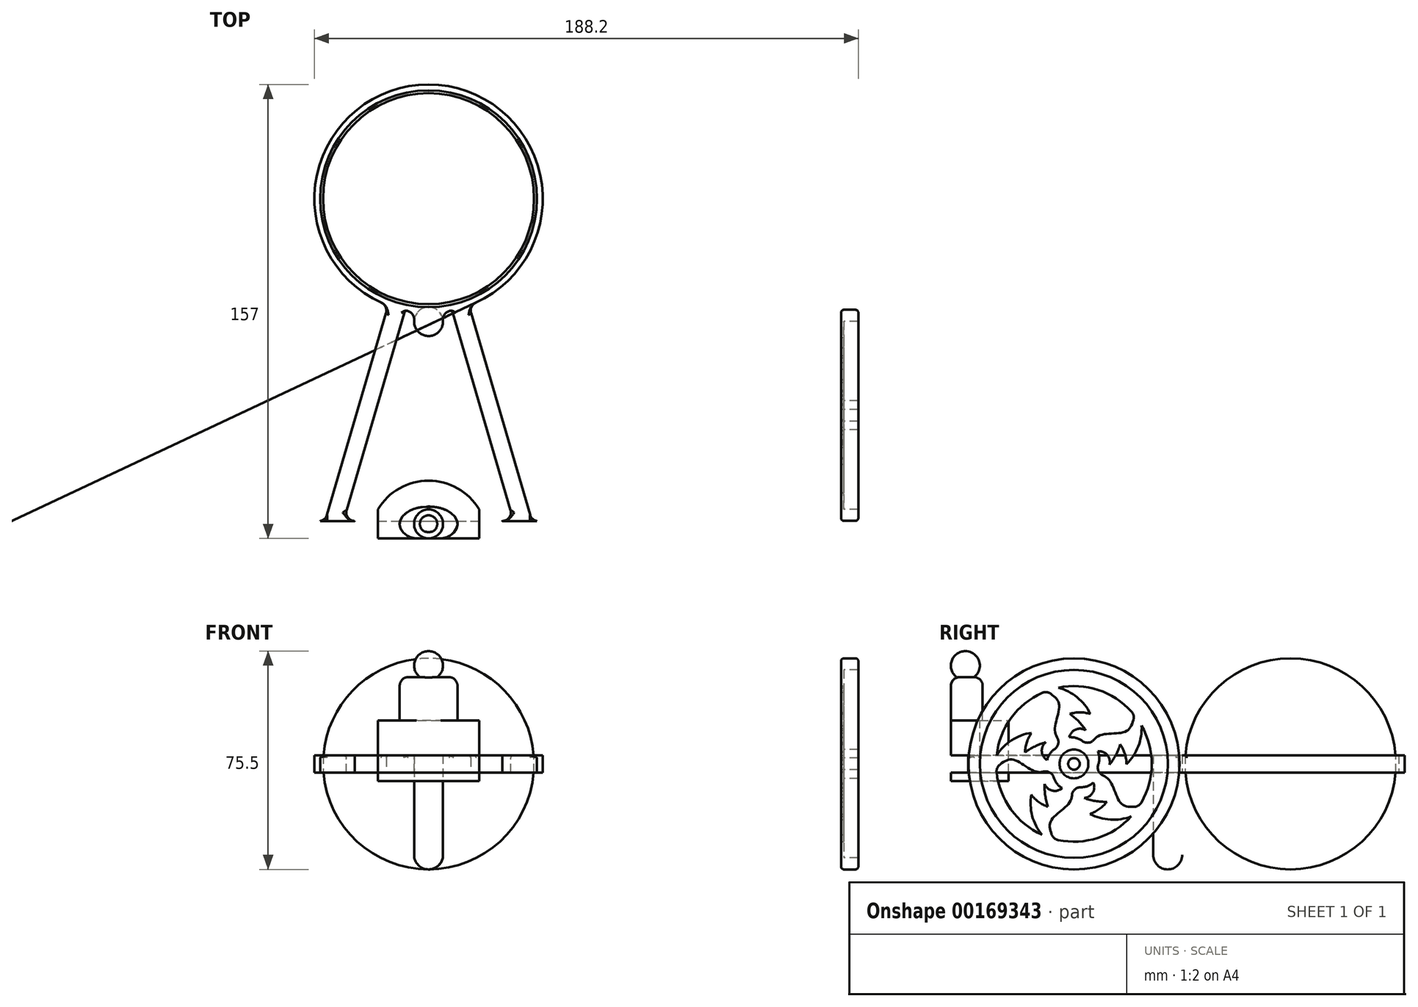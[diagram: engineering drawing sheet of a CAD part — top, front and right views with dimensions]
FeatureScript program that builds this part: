
annotation { "Feature Type Name" : "Feature", "Feature Type Description" : "" }
export const myFeature = defineFeature(function(context is Context, id is Id, definition is map)
    precondition{}
    {
        {
            var Q0;
            Q0=qCreatedBy(makeId("Front.planeOp"),FACE);
            var sketch = newSketch(context, id + "F0", { "sketchPlane" : qUnion([Q0])});
            skArc(sketch, "E0", {"start": v(0, 0) * mm, "mid": v(36.5, 36.5) * mm, "end": v(0, 73) * mm});
            skLineSegment(sketch, "E1", {"start": v(0, 73) * mm, "end": v(0, 0) * mm});
            skSolve(sketch);
        }
        {
            var Q0;
            Q0 = qSketchRegion(id + "F0", true);
            var Q1;
            Q1=sQuery(id+"F0.wireOp",EDGE,"E1");
            revolve(context, id + "F1", {"entities" : qUnion([Q0]), "axis" : qUnion([Q1]), "revolveType" : RevolveType.FULL});
        }
        {
            var Q0;
            Q0=qCreatedBy(makeId("Top.planeOp"),FACE);
            var sketch = newSketch(context, id + "F2", { "sketchPlane" : qUnion([Q0])});
            skCircle(sketch, "E2", {"center": v(0, 0) * mm, "radius": 37.5 * mm});
            skCircle(sketch, "E3.0", {"center": v(0, 0) * mm, "radius": 39.5 * mm});
            skLineSegment(sketch, "E4", {"start": v(0, 0) * mm, "end": v(-33.5, -114.5) * mm});
            skLineSegment(sketch, "E5", {"start": v(-33.5, -114.5) * mm, "end": v(33.5, -114.5) * mm});
            skLineSegment(sketch, "E6", {"start": v(33.5, -114.5) * mm, "end": v(0, 0) * mm});
            skLineSegment(sketch, "E7", {"start": v(0, 0) * mm, "end": v(0, 0) * mm});
            skLineSegment(sketch, "E8", {"start": v(0, 10.68) * mm, "end": v(-37.5, -117.5) * mm});
            skLineSegment(sketch, "E9", {"start": v(-37.5, -117.5) * mm, "end": v(37.5, -117.5) * mm});
            skLineSegment(sketch, "E10", {"start": v(37.5, -117.5) * mm, "end": v(0, 10.68) * mm});
            skLineSegment(sketch, "E11.0", {"start": v(0, -10.68) * mm, "end": v(-29.5, -111.5) * mm});
            skLineSegment(sketch, "E11.1", {"start": v(29.5, -111.5) * mm, "end": v(0, -10.68) * mm});
            skLineSegment(sketch, "E11.2", {"start": v(-29.5, -111.5) * mm, "end": v(29.5, -111.5) * mm});
            skLineSegment(sketch, "E12.top", {"start": v(-37.5, -111.5) * mm, "end": v(37.5, -111.5) * mm});
            skLineSegment(sketch, "E12.left", {"start": v(-37.5, -111.5) * mm, "end": v(-37.5, -117.5) * mm});
            skLineSegment(sketch, "E12.right", {"start": v(37.5, -111.5) * mm, "end": v(37.5, -117.5) * mm});
            skCircle(sketch, "E13", {"center": v(0, -42.5) * mm, "radius": 5 * mm});
            skSolve(sketch);
        }
        {
            var Q0;
            {var subQ0=sQuery(id+"F2.wireOp",EDGE,"E8");var subQ1=sQuery(id+"F2.wireOp",EDGE,"E2");var subQ2=makeQuery(id+"F2.imprint","INTERSECT",VERTEX,{"derivedFrom":[subQ1,subQ0]});Q0=makeQuery(id+"F2.imprint","IMPRINT",FACE,{"disambiguationData":[TD([[makeQuery(id+"F2.imprint","IMPRINT",EDGE,{"disambiguationData":[TD([[subQ2,1.0]])],"derivedFrom":subQ1}),-1.0]])]});}
            var Q1;
            {var subQ0=sQuery(id+"F2.wireOp",EDGE,"E8");var subQ1=sQuery(id+"F2.wireOp",EDGE,"E3.0");var subQ2=makeQuery(id+"F2.imprint","INTERSECT",VERTEX,{"derivedFrom":[subQ1,subQ0]});Q1=makeQuery(id+"F2.imprint","IMPRINT",FACE,{"disambiguationData":[TD([[makeQuery(id+"F2.imprint","IMPRINT",EDGE,{"disambiguationData":[TD([[subQ2,-1.0]])],"derivedFrom":subQ1}),-1.0]])]});}
            var Q2;
            {var subQ0=sQuery(id+"F2.wireOp",EDGE,"E4");var subQ1=sQuery(id+"F2.wireOp",EDGE,"E3.0");var subQ2=makeQuery(id+"F2.imprint","INTERSECT",VERTEX,{"derivedFrom":[subQ1,subQ0]});Q2=makeQuery(id+"F2.imprint","IMPRINT",FACE,{"disambiguationData":[TD([[makeQuery(id+"F2.imprint","IMPRINT",EDGE,{"disambiguationData":[TD([[subQ2,-1.0]])],"derivedFrom":subQ1}),-1.0]])]});}
            var Q3;
            {var subQ0=sQuery(id+"F2.wireOp",EDGE,"E12.left");Q3=makeQuery(id+"F2.imprint","IMPRINT",FACE,{"disambiguationData":[TD([[makeQuery(id+"F2.imprint","IMPRINT",EDGE,{"derivedFrom":subQ0}),1.0]])]});}
            var Q4;
            {var subQ1=sQuery(id+"F2.wireOp",EDGE,"E5");Q4=makeQuery(id+"F2.imprint","IMPRINT",FACE,{"disambiguationData":[TD([[makeQuery(id+"F2.imprint","IMPRINT",EDGE,{"derivedFrom":subQ1}),-1.0]])]});}
            var Q5;
            {var subQ0=sQuery(id+"F2.wireOp",EDGE,"E12.right");Q5=makeQuery(id+"F2.imprint","IMPRINT",FACE,{"disambiguationData":[TD([[makeQuery(id+"F2.imprint","IMPRINT",EDGE,{"derivedFrom":subQ0}),-1.0]])]});}
            var Q6;
            {var subQ1=sQuery(id+"F2.wireOp",EDGE,"E5");Q6=makeQuery(id+"F2.imprint","IMPRINT",FACE,{"disambiguationData":[TD([[makeQuery(id+"F2.imprint","IMPRINT",EDGE,{"derivedFrom":subQ1}),1.0]])]});}
            var Q7;
            {var subQ0=sQuery(id+"F2.wireOp",EDGE,"E11.1");var subQ1=sQuery(id+"F2.wireOp",EDGE,"E3.0");var subQ2=makeQuery(id+"F2.imprint","INTERSECT",VERTEX,{"derivedFrom":[subQ1,subQ0]});Q7=makeQuery(id+"F2.imprint","IMPRINT",FACE,{"disambiguationData":[TD([[makeQuery(id+"F2.imprint","IMPRINT",EDGE,{"disambiguationData":[TD([[subQ2,-1.0]])],"derivedFrom":subQ1}),-1.0]])]});}
            var Q8;
            {var subQ0=sQuery(id+"F2.wireOp",EDGE,"E10");var subQ1=sQuery(id+"F2.wireOp",EDGE,"E3.0");var subQ2=makeQuery(id+"F2.imprint","INTERSECT",VERTEX,{"derivedFrom":[subQ1,subQ0]});Q8=makeQuery(id+"F2.imprint","IMPRINT",FACE,{"disambiguationData":[TD([[makeQuery(id+"F2.imprint","IMPRINT",EDGE,{"disambiguationData":[TD([[subQ2,1.0]])],"derivedFrom":subQ1}),-1.0]])]});}
            var Q9;
            {var subQ0=sQuery(id+"F2.wireOp",EDGE,"E4");var subQ1=sQuery(id+"F2.wireOp",EDGE,"E2");var subQ2=makeQuery(id+"F2.imprint","INTERSECT",VERTEX,{"derivedFrom":[subQ1,subQ0]});Q9=makeQuery(id+"F2.imprint","IMPRINT",FACE,{"disambiguationData":[TD([[makeQuery(id+"F2.imprint","IMPRINT",EDGE,{"disambiguationData":[TD([[subQ2,-1.0]])],"derivedFrom":subQ1}),-1.0]])]});}
            var Q10;
            {var subQ0=sQuery(id+"F2.wireOp",EDGE,"E11.0");var subQ1=sQuery(id+"F2.wireOp",EDGE,"E2");var subQ2=makeQuery(id+"F2.imprint","INTERSECT",VERTEX,{"derivedFrom":[subQ1,subQ0]});Q10=makeQuery(id+"F2.imprint","IMPRINT",FACE,{"disambiguationData":[TD([[makeQuery(id+"F2.imprint","IMPRINT",EDGE,{"disambiguationData":[TD([[subQ2,-1.0]])],"derivedFrom":subQ1}),-1.0]])]});}
            var Q11;
            {var subQ0=sQuery(id+"F2.wireOp",EDGE,"E4");var subQ1=sQuery(id+"F2.wireOp",EDGE,"E2");var subQ2=makeQuery(id+"F2.imprint","INTERSECT",VERTEX,{"derivedFrom":[subQ1,subQ0]});Q11=makeQuery(id+"F2.imprint","IMPRINT",FACE,{"disambiguationData":[TD([[makeQuery(id+"F2.imprint","IMPRINT",EDGE,{"disambiguationData":[TD([[subQ2,1.0]])],"derivedFrom":subQ1}),-1.0]])]});}
            var Q12;
            {var subQ0=sQuery(id+"F2.wireOp",EDGE,"E13");var subQ1=sQuery(id+"F2.wireOp",EDGE,"E2");var subQ2=makeQuery(id+"F2.imprint","INTERSECT",VERTEX,{"derivedFrom":[subQ1,subQ0]});Q12=makeQuery(id+"F2.imprint","IMPRINT",FACE,{"disambiguationData":[TD([[makeQuery(id+"F2.imprint","IMPRINT",EDGE,{"disambiguationData":[TD([[subQ2,-1.0]])],"derivedFrom":subQ1}),-1.0]])]});}
            var Q13;
            {var subQ0=sQuery(id+"F2.wireOp",EDGE,"E13");var subQ1=sQuery(id+"F2.wireOp",EDGE,"E3.0");var subQ2=makeQuery(id+"F2.imprint","INTERSECT",VERTEX,{"disambiguationData":[OD(0.0)],"derivedFrom":[subQ1,subQ0]});Q13=makeQuery(id+"F2.imprint","IMPRINT",FACE,{"disambiguationData":[TD([[makeQuery(id+"F2.imprint","IMPRINT",EDGE,{"disambiguationData":[TD([[subQ2,-1.0]])],"derivedFrom":subQ1}),1.0]])]});}
            var Q14;
            {var subQ0=sQuery(id+"F2.wireOp",EDGE,"E11.1");var subQ1=sQuery(id+"F2.wireOp",EDGE,"E2");var subQ2=makeQuery(id+"F2.imprint","INTERSECT",VERTEX,{"derivedFrom":[subQ1,subQ0]});Q14=makeQuery(id+"F2.imprint","IMPRINT",FACE,{"disambiguationData":[TD([[makeQuery(id+"F2.imprint","IMPRINT",EDGE,{"disambiguationData":[TD([[subQ2,-1.0]])],"derivedFrom":subQ1}),-1.0]])]});}
            var Q15;
            {var subQ0=sQuery(id+"F2.wireOp",EDGE,"E6");var subQ1=sQuery(id+"F2.wireOp",EDGE,"E2");var subQ2=makeQuery(id+"F2.imprint","INTERSECT",VERTEX,{"derivedFrom":[subQ1,subQ0]});Q15=makeQuery(id+"F2.imprint","IMPRINT",FACE,{"disambiguationData":[TD([[makeQuery(id+"F2.imprint","IMPRINT",EDGE,{"disambiguationData":[TD([[subQ2,-1.0]])],"derivedFrom":subQ1}),-1.0]])]});}
            extrude(context, id + "F3", {"entities" : qUnion([Q0, Q1, Q2, Q3, Q4, Q5, Q6, Q7, Q8, Q9, Q10, Q11, Q12, Q13, Q14, Q15]), "depth" : 39.5 * mm, "hasSecondDirection" : true, "secondDirectionOppositeDirection" : false, "secondDirectionDepth" : 33.5 * mm});
        }
        {
            var Q0;
            {var subQ0=sQuery(id+"F2.wireOp",EDGE,"E13");var subQ1=sQuery(id+"F2.wireOp",EDGE,"E3.0");var subQ2=makeQuery(id+"F2.imprint","INTERSECT",VERTEX,{"disambiguationData":[OD(0.0)],"derivedFrom":[subQ1,subQ0]});Q0=makeQuery(id+"F2.imprint","IMPRINT",FACE,{"disambiguationData":[TD([[makeQuery(id+"F2.imprint","IMPRINT",EDGE,{"disambiguationData":[TD([[subQ2,-1.0]])],"derivedFrom":subQ1}),-1.0]])]});}
            var Q1;
            {var subQ0=sQuery(id+"F2.wireOp",EDGE,"E13");var subQ1=sQuery(id+"F2.wireOp",EDGE,"E3.0");var subQ2=makeQuery(id+"F2.imprint","INTERSECT",VERTEX,{"disambiguationData":[OD(0.0)],"derivedFrom":[subQ1,subQ0]});Q1=makeQuery(id+"F2.imprint","IMPRINT",FACE,{"disambiguationData":[TD([[makeQuery(id+"F2.imprint","IMPRINT",EDGE,{"disambiguationData":[TD([[subQ2,-1.0]])],"derivedFrom":subQ1}),1.0]])]});}
            extrude(context, id + "F4", {"entities" : qUnion([Q0, Q1]), "operationType" : NewBodyOperationType.ADD, "depth" : 39.5 * mm});
        }
        {
            var Q0;
            Q0=makeQuery(id+"F4.opExtrude","CAP_EDGE",EDGE,{"disambiguationData":[OSD([sQuery(id+"F2.wireOp",EDGE,"E13")])],"isStart":true});
            fillet(context, id + "F5", {"entities" : qUnion([Q0]), "radius" : 5 * mm, "tangentPropagation" : true, "allowEdgeOverflow" : false});
        }
        {
            var Q0;
            Q0=qCreatedBy(makeId("Right.planeOp"),FACE);
            var sketch = newSketch(context, id + "F6", { "sketchPlane" : qUnion([Q0])});
            skCircle(sketch, "E14", {"center": v(-114.5, 36.5) * mm, "radius": 36.5 * mm});
            skCircle(sketch, "E15", {"center": v(-114.5, 36.5) * mm, "radius": 1.9 * mm});
            skLineSegment(sketch, "E16", {"start": v(-114.5, 36.5) * mm, "end": v(-114.5, 41.97) * mm, "construction": true});
            skLineSegment(sketch, "E17", {"start": v(-114.5, 36.5) * mm, "end": v(-121.58, 36.5) * mm, "construction": true});
            skSolve(sketch);
        }
        {
            var Q0;
            Q0=makeQuery(id+"F6.imprint","IMPRINT",FACE,{"disambiguationData":[TD([[makeQuery(id+"F6.imprint","IMPRINT",EDGE,{"derivedFrom":sQuery(id+"F6.wireOp",EDGE,"E15")}),1.0]])]});
            extrude(context, id + "F7", {"entities" : qUnion([Q0]), "operationType" : NewBodyOperationType.ADD, "depth" : 45.5 * mm, "hasSecondDirection" : true, "secondDirectionOppositeDirection" : true, "secondDirectionDepth" : 45.5 * mm});
        }
        {
            var Q0;
            Q0=makeQuery(id+"F3.opExtrude","CAP_FACE",FACE,{"disambiguationData":[OSD([sQuery(id+"F2.wireOp",EDGE,"E2"),sQuery(id+"F2.wireOp",EDGE,"E3.0"),sQuery(id+"F2.wireOp",EDGE,"E8"),sQuery(id+"F2.wireOp",EDGE,"E10"),sQuery(id+"F2.wireOp",EDGE,"E11.0"),sQuery(id+"F2.wireOp",EDGE,"E11.1"),sQuery(id+"F2.wireOp",EDGE,"E9"),sQuery(id+"F2.wireOp",EDGE,"E12.top"),sQuery(id+"F2.wireOp",EDGE,"E12.left"),sQuery(id+"F2.wireOp",EDGE,"E12.right")])],"isStart":true});
            var Q1;
            Q1=makeQuery(id+"F4.boolean.opBoolean","MERGE",FACE,{"derivedFrom":[makeQuery(id+"F3.opExtrude","CAP_FACE",FACE,{"disambiguationData":[OSD([sQuery(id+"F2.wireOp",EDGE,"E2"),sQuery(id+"F2.wireOp",EDGE,"E3.0"),sQuery(id+"F2.wireOp",EDGE,"E8"),sQuery(id+"F2.wireOp",EDGE,"E10"),sQuery(id+"F2.wireOp",EDGE,"E11.0"),sQuery(id+"F2.wireOp",EDGE,"E11.1"),sQuery(id+"F2.wireOp",EDGE,"E9"),sQuery(id+"F2.wireOp",EDGE,"E12.top"),sQuery(id+"F2.wireOp",EDGE,"E12.left"),sQuery(id+"F2.wireOp",EDGE,"E12.right")])],"isStart":false}),makeQuery(id+"F4.opExtrude","CAP_FACE",FACE,{"disambiguationData":[OSD([sQuery(id+"F2.wireOp",EDGE,"E13")])],"isStart":false})]});
            cPlane(context, id + "F8", {"entities" : qUnion([Q0, Q1]), "cplaneType" : CPlaneType.MID_PLANE, "offset" : 25.4 * mm, "width" : 152.4 * mm, "height" : 152.4 * mm});
        }
        {
            var Q0;
            Q0=qCreatedBy(makeId("Right.planeOp"),FACE);
            var sketch = newSketch(context, id + "F9", { "sketchPlane" : qUnion([Q0])});
            skCircle(sketch, "E18", {"center": v(-114.5, 36.5) * mm, "radius": 2.25 * mm});
            skLineSegment(sketch, "E19", {"start": v(-116.25, 37.92) * mm, "end": v(-112.75, 37.92) * mm});
            skLineSegment(sketch, "E20", {"start": v(-116.47, 35.42) * mm, "end": v(-112.53, 35.42) * mm});
            skLineSegment(sketch, "E21", {"start": v(-115, 38.7) * mm, "end": v(-115, 34.3) * mm});
            skLineSegment(sketch, "E22", {"start": v(-114, 38.7) * mm, "end": v(-114, 34.3) * mm});
            skLineSegment(sketch, "E23", {"start": v(-114.5, 36.5) * mm, "end": v(-114.5, 31.41) * mm, "construction": true});
            skSolve(sketch);
        }
        {
            var Q0;
            {var subQ0=sQuery(id+"F9.wireOp",EDGE,"E19");var subQ1=sQuery(id+"F9.wireOp",EDGE,"E18");var subQ2=makeQuery(id+"F9.imprint","INTERSECT",VERTEX,{"disambiguationData":[OD(0.0)],"derivedFrom":[subQ1,subQ0]});Q0=makeQuery(id+"F9.imprint","IMPRINT",FACE,{"disambiguationData":[TD([[makeQuery(id+"F9.imprint","IMPRINT",EDGE,{"disambiguationData":[TD([[subQ2,-1.0]])],"derivedFrom":subQ1}),1.0]])]});}
            var Q1;
            {var subQ0=sQuery(id+"F9.wireOp",EDGE,"E19");var subQ1=sQuery(id+"F9.wireOp",EDGE,"E18");var subQ2=makeQuery(id+"F9.imprint","INTERSECT",VERTEX,{"disambiguationData":[OD(1.0)],"derivedFrom":[subQ1,subQ0]});Q1=makeQuery(id+"F9.imprint","IMPRINT",FACE,{"disambiguationData":[TD([[makeQuery(id+"F9.imprint","IMPRINT",EDGE,{"disambiguationData":[TD([[subQ2,1.0]])],"derivedFrom":subQ1}),1.0]])]});}
            var Q2;
            {var subQ0=sQuery(id+"F9.wireOp",EDGE,"E21");var subQ1=sQuery(id+"F9.wireOp",EDGE,"E19");var subQ2=makeQuery(id+"F9.imprint","INTERSECT",VERTEX,{"derivedFrom":[subQ1,subQ0]});Q2=makeQuery(id+"F9.imprint","IMPRINT",FACE,{"disambiguationData":[TD([[makeQuery(id+"F9.imprint","IMPRINT",EDGE,{"disambiguationData":[TD([[subQ2,-1.0]])],"derivedFrom":subQ1}),-1.0]])]});}
            var Q3;
            Q3=makeQuery(id+"F7.opExtrude","CAP_FACE",FACE,{"disambiguationData":[OSD([sQuery(id+"F6.wireOp",EDGE,"E15")])],"isStart":false});
            extrude(context, id + "F10", {"entities" : qUnion([Q0, Q1, Q2]), "operationType" : NewBodyOperationType.ADD, "endBound" : BoundingType.UP_TO_SURFACE, "endBoundEntityFace" : qUnion([Q3]), "depth" : 25.4 * mm, "hasSecondDirection" : true, "secondDirectionOppositeDirection" : false, "secondDirectionDepth" : 44 * mm});
        }
        {
            var Q0;
            {var subQ0=sQuery(id+"F9.wireOp",EDGE,"E19");var subQ1=sQuery(id+"F9.wireOp",EDGE,"E18");var subQ2=makeQuery(id+"F9.imprint","INTERSECT",VERTEX,{"disambiguationData":[OD(0.0)],"derivedFrom":[subQ1,subQ0]});Q0=makeQuery(id+"F9.imprint","IMPRINT",FACE,{"disambiguationData":[TD([[makeQuery(id+"F9.imprint","IMPRINT",EDGE,{"disambiguationData":[TD([[subQ2,-1.0]])],"derivedFrom":subQ1}),1.0]])]});}
            var Q1;
            {var subQ0=sQuery(id+"F9.wireOp",EDGE,"E21");var subQ1=sQuery(id+"F9.wireOp",EDGE,"E19");var subQ2=makeQuery(id+"F9.imprint","INTERSECT",VERTEX,{"derivedFrom":[subQ1,subQ0]});Q1=makeQuery(id+"F9.imprint","IMPRINT",FACE,{"disambiguationData":[TD([[makeQuery(id+"F9.imprint","IMPRINT",EDGE,{"disambiguationData":[TD([[subQ2,-1.0]])],"derivedFrom":subQ1}),-1.0]])]});}
            var Q2;
            {var subQ0=sQuery(id+"F9.wireOp",EDGE,"E19");var subQ1=sQuery(id+"F9.wireOp",EDGE,"E18");var subQ2=makeQuery(id+"F9.imprint","INTERSECT",VERTEX,{"disambiguationData":[OD(1.0)],"derivedFrom":[subQ1,subQ0]});Q2=makeQuery(id+"F9.imprint","IMPRINT",FACE,{"disambiguationData":[TD([[makeQuery(id+"F9.imprint","IMPRINT",EDGE,{"disambiguationData":[TD([[subQ2,1.0]])],"derivedFrom":subQ1}),1.0]])]});}
            var Q3;
            Q3=makeQuery(id+"F7.opExtrude","CAP_FACE",FACE,{"disambiguationData":[OSD([sQuery(id+"F6.wireOp",EDGE,"E15")])],"isStart":true});
            extrude(context, id + "F11", {"entities" : qUnion([Q0, Q1, Q2]), "operationType" : NewBodyOperationType.ADD, "endBound" : BoundingType.UP_TO_SURFACE, "oppositeDirection" : true, "endBoundEntityFace" : qUnion([Q3]), "depth" : 25.4 * mm, "hasSecondDirection" : true, "secondDirectionOppositeDirection" : true, "secondDirectionDepth" : 44 * mm});
        }
        {
            var Q0;
            {var subQ0=sQuery(id+"F9.wireOp",EDGE,"E21");var subQ1=sQuery(id+"F9.wireOp",EDGE,"E18");var subQ2=makeQuery(id+"F9.imprint","INTERSECT",VERTEX,{"disambiguationData":[OD(0.0)],"derivedFrom":[subQ1,subQ0]});Q0=makeQuery(id+"F9.imprint","IMPRINT",FACE,{"disambiguationData":[TD([[makeQuery(id+"F9.imprint","IMPRINT",EDGE,{"disambiguationData":[TD([[subQ2,1.0]])],"derivedFrom":subQ1}),1.0]])]});}
            var Q1;
            {var subQ0=sQuery(id+"F9.wireOp",EDGE,"E21");var subQ1=sQuery(id+"F9.wireOp",EDGE,"E19");var subQ2=makeQuery(id+"F9.imprint","INTERSECT",VERTEX,{"derivedFrom":[subQ1,subQ0]});Q1=makeQuery(id+"F9.imprint","IMPRINT",FACE,{"disambiguationData":[TD([[makeQuery(id+"F9.imprint","IMPRINT",EDGE,{"disambiguationData":[TD([[subQ2,-1.0]])],"derivedFrom":subQ1}),-1.0]])]});}
            var Q2;
            {var subQ0=sQuery(id+"F9.wireOp",EDGE,"E21");var subQ1=sQuery(id+"F9.wireOp",EDGE,"E18");var subQ2=makeQuery(id+"F9.imprint","INTERSECT",VERTEX,{"disambiguationData":[OD(1.0)],"derivedFrom":[subQ1,subQ0]});Q2=makeQuery(id+"F9.imprint","IMPRINT",FACE,{"disambiguationData":[TD([[makeQuery(id+"F9.imprint","IMPRINT",EDGE,{"disambiguationData":[TD([[subQ2,-1.0]])],"derivedFrom":subQ1}),1.0]])]});}
            var Q3;
            Q3=makeQuery(id+"F10.boolean.opBoolean","MERGE",FACE,{"derivedFrom":[makeQuery(id+"F7.opExtrude","CAP_FACE",FACE,{"disambiguationData":[OSD([sQuery(id+"F6.wireOp",EDGE,"E15")])],"isStart":false}),makeQuery(id+"F10.opExtrude","CAP_FACE",FACE,{"disambiguationData":[OSD([sQuery(id+"F9.wireOp",EDGE,"E18"),sQuery(id+"F9.wireOp",EDGE,"E19"),sQuery(id+"F9.wireOp",EDGE,"E20")])],"isStart":false})]});
            extrude(context, id + "F12", {"entities" : qUnion([Q0, Q1, Q2]), "operationType" : NewBodyOperationType.REMOVE, "endBound" : BoundingType.UP_TO_SURFACE, "endBoundEntityFace" : qUnion([Q3]), "depth" : 25.4 * mm, "hasSecondDirection" : true, "secondDirectionOppositeDirection" : false, "secondDirectionDepth" : 40 * mm});
        }
        {
            var Q0;
            {var subQ0=sQuery(id+"F9.wireOp",EDGE,"E21");var subQ1=sQuery(id+"F9.wireOp",EDGE,"E18");var subQ2=makeQuery(id+"F9.imprint","INTERSECT",VERTEX,{"disambiguationData":[OD(0.0)],"derivedFrom":[subQ1,subQ0]});Q0=makeQuery(id+"F9.imprint","IMPRINT",FACE,{"disambiguationData":[TD([[makeQuery(id+"F9.imprint","IMPRINT",EDGE,{"disambiguationData":[TD([[subQ2,1.0]])],"derivedFrom":subQ1}),1.0]])]});}
            var Q1;
            {var subQ0=sQuery(id+"F9.wireOp",EDGE,"E21");var subQ1=sQuery(id+"F9.wireOp",EDGE,"E19");var subQ2=makeQuery(id+"F9.imprint","INTERSECT",VERTEX,{"derivedFrom":[subQ1,subQ0]});Q1=makeQuery(id+"F9.imprint","IMPRINT",FACE,{"disambiguationData":[TD([[makeQuery(id+"F9.imprint","IMPRINT",EDGE,{"disambiguationData":[TD([[subQ2,-1.0]])],"derivedFrom":subQ1}),-1.0]])]});}
            var Q2;
            {var subQ0=sQuery(id+"F9.wireOp",EDGE,"E21");var subQ1=sQuery(id+"F9.wireOp",EDGE,"E18");var subQ2=makeQuery(id+"F9.imprint","INTERSECT",VERTEX,{"disambiguationData":[OD(1.0)],"derivedFrom":[subQ1,subQ0]});Q2=makeQuery(id+"F9.imprint","IMPRINT",FACE,{"disambiguationData":[TD([[makeQuery(id+"F9.imprint","IMPRINT",EDGE,{"disambiguationData":[TD([[subQ2,-1.0]])],"derivedFrom":subQ1}),1.0]])]});}
            var Q3;
            Q3=makeQuery(id+"F11.boolean.opBoolean","MERGE",FACE,{"derivedFrom":[makeQuery(id+"F7.opExtrude","CAP_FACE",FACE,{"disambiguationData":[OSD([sQuery(id+"F6.wireOp",EDGE,"E15")])],"isStart":true}),makeQuery(id+"F11.opExtrude","CAP_FACE",FACE,{"disambiguationData":[OSD([sQuery(id+"F9.wireOp",EDGE,"E18"),sQuery(id+"F9.wireOp",EDGE,"E19"),sQuery(id+"F9.wireOp",EDGE,"E20")])],"isStart":false})]});
            extrude(context, id + "F13", {"entities" : qUnion([Q0, Q1, Q2]), "operationType" : NewBodyOperationType.REMOVE, "endBound" : BoundingType.UP_TO_SURFACE, "oppositeDirection" : true, "endBoundEntityFace" : qUnion([Q3]), "depth" : 25.4 * mm, "hasSecondDirection" : true, "secondDirectionOppositeDirection" : true, "secondDirectionDepth" : 40 * mm});
        }
        {
            var Q0;
            Q0=makeQuery(id+"F3.opExtrude","CAP_EDGE",EDGE,{"disambiguationData":[OSD([sQuery(id+"F2.wireOp",EDGE,"E9")])],"isStart":false});
            var Q1;
            {var subQ0=sQuery(id+"F2.wireOp",EDGE,"E12.top");Q1=makeQuery(id+"F3.opExtrude","CAP_EDGE",EDGE,{"disambiguationData":[OSD([subQ0]),TDD([makeQuery(id+"F2.imprint","IMPRINT",EDGE,{"disambiguationData":[TD([[makeQuery(id+"F2.imprint","INTERSECT",VERTEX,{"derivedFrom":[sQuery(id+"F2.wireOp",EDGE,"E11.0"),subQ0]}),-1.0]])],"derivedFrom":subQ0})])],"isStart":false});}
            var Q2;
            {var subQ0=sQuery(id+"F2.wireOp",EDGE,"E12.top");Q2=makeQuery(id+"F3.opExtrude","CAP_EDGE",EDGE,{"disambiguationData":[OSD([subQ0]),TDD([makeQuery(id+"F2.imprint","IMPRINT",EDGE,{"disambiguationData":[TD([[makeQuery(id+"F2.imprint","INTERSECT",VERTEX,{"derivedFrom":[subQ0,sQuery(id+"F2.wireOp",EDGE,"E12.left")]}),-1.0]])],"derivedFrom":subQ0})])],"isStart":false});}
            var Q3;
            {var subQ0=sQuery(id+"F2.wireOp",EDGE,"E12.top");Q3=makeQuery(id+"F3.opExtrude","CAP_EDGE",EDGE,{"disambiguationData":[OSD([subQ0]),TDD([makeQuery(id+"F2.imprint","IMPRINT",EDGE,{"disambiguationData":[TD([[makeQuery(id+"F2.imprint","INTERSECT",VERTEX,{"derivedFrom":[subQ0,sQuery(id+"F2.wireOp",EDGE,"E12.right")]}),1.0]])],"derivedFrom":subQ0})])],"isStart":false});}
            var Q4;
            Q4=makeQuery(id+"F3.opExtrude","CAP_EDGE",EDGE,{"disambiguationData":[OSD([sQuery(id+"F2.wireOp",EDGE,"E10")])],"isStart":false});
            var Q5;
            Q5=makeQuery(id+"F3.opExtrude","CAP_EDGE",EDGE,{"disambiguationData":[OSD([sQuery(id+"F2.wireOp",EDGE,"E11.1")])],"isStart":false});
            var Q6;
            Q6=makeQuery(id+"F3.opExtrude","CAP_EDGE",EDGE,{"disambiguationData":[OSD([sQuery(id+"F2.wireOp",EDGE,"E8")])],"isStart":false});
            var Q7;
            Q7=makeQuery(id+"F3.opExtrude","CAP_EDGE",EDGE,{"disambiguationData":[OSD([sQuery(id+"F2.wireOp",EDGE,"E11.0")])],"isStart":false});
            fillet(context, id + "F14", {"entities" : qUnion([Q0, Q1, Q2, Q3, Q4, Q5, Q6, Q7]), "radius" : 1 * mm, "tangentPropagation" : true, "allowEdgeOverflow" : false});
        }
        {
            var Q0;
            {var subQ0=sQuery(id+"F2.wireOp",EDGE,"E13");var subQ1=sQuery(id+"F2.wireOp",EDGE,"E3.0");var subQ2=makeQuery(id+"F2.imprint","INTERSECT",VERTEX,{"disambiguationData":[OD(1.0)],"derivedFrom":[subQ1,subQ0]});var subQ3=makeQuery(id+"F2.imprint","INTERSECT",VERTEX,{"disambiguationData":[OD(0.0)],"derivedFrom":[subQ1,subQ0]});Q0=makeQuery(id+"F4.boolean.opBoolean","INTERSECT",EDGE,{"disambiguationData":[OD(0.0)],"derivedFrom":[makeQuery(id+"F3.opExtrude","SWEPT_FACE",FACE,{"disambiguationData":[OSD([subQ1]),TDD([makeQuery(id+"F2.imprint","IMPRINT",EDGE,{"disambiguationData":[TD([[makeQuery(id+"F2.imprint","INTERSECT",VERTEX,{"derivedFrom":[subQ1,sQuery(id+"F2.wireOp",EDGE,"E11.0")]}),-1.0]])],"derivedFrom":subQ1}),makeQuery(id+"F2.imprint","IMPRINT",EDGE,{"disambiguationData":[TD([[subQ3,-1.0]])],"derivedFrom":subQ1}),makeQuery(id+"F2.imprint","IMPRINT",EDGE,{"disambiguationData":[TD([[subQ2,-1.0]])],"derivedFrom":subQ1})])]}),makeQuery(id+"F4.opExtrude","SWEPT_FACE",FACE,{"disambiguationData":[OSD([subQ0])]})]});}
            var Q1;
            {var subQ0=sQuery(id+"F2.wireOp",EDGE,"E13");var subQ1=sQuery(id+"F2.wireOp",EDGE,"E3.0");var subQ2=makeQuery(id+"F2.imprint","INTERSECT",VERTEX,{"disambiguationData":[OD(1.0)],"derivedFrom":[subQ1,subQ0]});var subQ3=makeQuery(id+"F2.imprint","INTERSECT",VERTEX,{"disambiguationData":[OD(0.0)],"derivedFrom":[subQ1,subQ0]});Q1=makeQuery(id+"F4.boolean.opBoolean","INTERSECT",EDGE,{"disambiguationData":[OD(1.0)],"derivedFrom":[makeQuery(id+"F3.opExtrude","SWEPT_FACE",FACE,{"disambiguationData":[OSD([subQ1]),TDD([makeQuery(id+"F2.imprint","IMPRINT",EDGE,{"disambiguationData":[TD([[makeQuery(id+"F2.imprint","INTERSECT",VERTEX,{"derivedFrom":[subQ1,sQuery(id+"F2.wireOp",EDGE,"E11.0")]}),-1.0]])],"derivedFrom":subQ1}),makeQuery(id+"F2.imprint","IMPRINT",EDGE,{"disambiguationData":[TD([[subQ3,-1.0]])],"derivedFrom":subQ1}),makeQuery(id+"F2.imprint","IMPRINT",EDGE,{"disambiguationData":[TD([[subQ2,-1.0]])],"derivedFrom":subQ1})])]}),makeQuery(id+"F4.opExtrude","SWEPT_FACE",FACE,{"disambiguationData":[OSD([subQ0])]})]});}
            fillet(context, id + "F15", {"entities" : qUnion([Q0, Q1]), "radius" : 3 * mm, "tangentPropagation" : true, "allowEdgeOverflow" : false});
        }
        {
            var Q0;
            Q0=makeQuery(id+"F3.opExtrude","SWEPT_EDGE",EDGE,{"disambiguationData":[OSD([sQuery(id+"F2.wireOp",EDGE,"E11.0"),sQuery(id+"F2.wireOp",EDGE,"E12.top")])]});
            var Q1;
            Q1=makeQuery(id+"F3.opExtrude","SWEPT_EDGE",EDGE,{"disambiguationData":[OSD([sQuery(id+"F2.wireOp",EDGE,"E11.1"),sQuery(id+"F2.wireOp",EDGE,"E12.top")])]});
            var Q2;
            Q2=makeQuery(id+"F3.opExtrude","SWEPT_EDGE",EDGE,{"disambiguationData":[OSD([sQuery(id+"F2.wireOp",EDGE,"E10"),sQuery(id+"F2.wireOp",EDGE,"E12.top")])]});
            var Q3;
            Q3=makeQuery(id+"F3.opExtrude","SWEPT_EDGE",EDGE,{"disambiguationData":[OSD([sQuery(id+"F2.wireOp",EDGE,"E8"),sQuery(id+"F2.wireOp",EDGE,"E12.top")])]});
            var Q4;
            Q4=makeQuery(id+"F3.opExtrude","SWEPT_EDGE",EDGE,{"disambiguationData":[OSD([sQuery(id+"F2.wireOp",EDGE,"E3.0"),sQuery(id+"F2.wireOp",EDGE,"E10")])]});
            var Q5;
            Q5=makeQuery(id+"F3.opExtrude","SWEPT_EDGE",EDGE,{"disambiguationData":[OSD([sQuery(id+"F2.wireOp",EDGE,"E3.0"),sQuery(id+"F2.wireOp",EDGE,"E8")])]});
            fillet(context, id + "F16", {"entities" : qUnion([Q0, Q1, Q2, Q3, Q4, Q5]), "radius" : 3 * mm, "tangentPropagation" : true, "allowEdgeOverflow" : false});
        }
        {
            var Q0;
            Q0=makeQuery(id+"F3.opExtrude","SWEPT_EDGE",EDGE,{"disambiguationData":[OSD([sQuery(id+"F2.wireOp",EDGE,"E3.0"),sQuery(id+"F2.wireOp",EDGE,"E11.0")])]});
            var Q1;
            Q1=makeQuery(id+"F3.opExtrude","SWEPT_EDGE",EDGE,{"disambiguationData":[OSD([sQuery(id+"F2.wireOp",EDGE,"E3.0"),sQuery(id+"F2.wireOp",EDGE,"E11.1")])]});
            fillet(context, id + "F17", {"entities" : qUnion([Q0, Q1]), "radius" : 1 * mm, "tangentPropagation" : true, "allowEdgeOverflow" : false});
        }
        {
            var Q0;
            {var subQ0=sQuery(id+"F9.wireOp",EDGE,"E18");Q0=makeQuery(id+"F10.opExtrude","CAP_EDGE",EDGE,{"disambiguationData":[OSD([subQ0]),TDD([makeQuery(id+"F9.imprint","IMPRINT",EDGE,{"disambiguationData":[TD([[makeQuery(id+"F9.imprint","INTERSECT",VERTEX,{"disambiguationData":[OD(0.0)],"derivedFrom":[subQ0,sQuery(id+"F9.wireOp",EDGE,"E19")]}),-1.0]])],"derivedFrom":subQ0})])],"isStart":false});}
            var Q1;
            {var subQ0=sQuery(id+"F9.wireOp",EDGE,"E18");Q1=makeQuery(id+"F10.opExtrude","CAP_EDGE",EDGE,{"disambiguationData":[OSD([subQ0]),TDD([makeQuery(id+"F9.imprint","IMPRINT",EDGE,{"disambiguationData":[TD([[makeQuery(id+"F9.imprint","INTERSECT",VERTEX,{"disambiguationData":[OD(1.0)],"derivedFrom":[subQ0,sQuery(id+"F9.wireOp",EDGE,"E19")]}),1.0]])],"derivedFrom":subQ0})])],"isStart":false});}
            var Q2;
            {var subQ0=sQuery(id+"F9.wireOp",EDGE,"E18");Q2=makeQuery(id+"F10.opExtrude","CAP_EDGE",EDGE,{"disambiguationData":[OSD([subQ0]),TDD([makeQuery(id+"F9.imprint","IMPRINT",EDGE,{"disambiguationData":[TD([[makeQuery(id+"F9.imprint","INTERSECT",VERTEX,{"disambiguationData":[OD(0.0)],"derivedFrom":[subQ0,sQuery(id+"F9.wireOp",EDGE,"E19")]}),-1.0]])],"derivedFrom":subQ0})])],"isStart":true});}
            var Q3;
            {var subQ0=sQuery(id+"F9.wireOp",EDGE,"E18");Q3=makeQuery(id+"F10.opExtrude","CAP_EDGE",EDGE,{"disambiguationData":[OSD([subQ0]),TDD([makeQuery(id+"F9.imprint","IMPRINT",EDGE,{"disambiguationData":[TD([[makeQuery(id+"F9.imprint","INTERSECT",VERTEX,{"disambiguationData":[OD(1.0)],"derivedFrom":[subQ0,sQuery(id+"F9.wireOp",EDGE,"E19")]}),1.0]])],"derivedFrom":subQ0})])],"isStart":true});}
            var Q4;
            {var subQ0=sQuery(id+"F9.wireOp",EDGE,"E18");Q4=makeQuery(id+"F11.opExtrude","CAP_EDGE",EDGE,{"disambiguationData":[OSD([subQ0]),TDD([makeQuery(id+"F9.imprint","IMPRINT",EDGE,{"disambiguationData":[TD([[makeQuery(id+"F9.imprint","INTERSECT",VERTEX,{"disambiguationData":[OD(0.0)],"derivedFrom":[subQ0,sQuery(id+"F9.wireOp",EDGE,"E19")]}),-1.0]])],"derivedFrom":subQ0})])],"isStart":false});}
            var Q5;
            {var subQ0=sQuery(id+"F9.wireOp",EDGE,"E18");Q5=makeQuery(id+"F11.opExtrude","CAP_EDGE",EDGE,{"disambiguationData":[OSD([subQ0]),TDD([makeQuery(id+"F9.imprint","IMPRINT",EDGE,{"disambiguationData":[TD([[makeQuery(id+"F9.imprint","INTERSECT",VERTEX,{"disambiguationData":[OD(0.0)],"derivedFrom":[subQ0,sQuery(id+"F9.wireOp",EDGE,"E19")]}),-1.0]])],"derivedFrom":subQ0})])],"isStart":true});}
            var Q6;
            {var subQ0=sQuery(id+"F9.wireOp",EDGE,"E18");Q6=makeQuery(id+"F11.opExtrude","CAP_EDGE",EDGE,{"disambiguationData":[OSD([subQ0]),TDD([makeQuery(id+"F9.imprint","IMPRINT",EDGE,{"disambiguationData":[TD([[makeQuery(id+"F9.imprint","INTERSECT",VERTEX,{"disambiguationData":[OD(1.0)],"derivedFrom":[subQ0,sQuery(id+"F9.wireOp",EDGE,"E19")]}),1.0]])],"derivedFrom":subQ0})])],"isStart":false});}
            var Q7;
            {var subQ0=sQuery(id+"F9.wireOp",EDGE,"E18");Q7=makeQuery(id+"F11.opExtrude","CAP_EDGE",EDGE,{"disambiguationData":[OSD([subQ0]),TDD([makeQuery(id+"F9.imprint","IMPRINT",EDGE,{"disambiguationData":[TD([[makeQuery(id+"F9.imprint","INTERSECT",VERTEX,{"disambiguationData":[OD(1.0)],"derivedFrom":[subQ0,sQuery(id+"F9.wireOp",EDGE,"E19")]}),1.0]])],"derivedFrom":subQ0})])],"isStart":true});}
            chamfer(context, id + "F18", {"entities" : qUnion([Q0, Q1, Q2, Q3, Q4, Q5, Q6, Q7]), "width" : .5 * mm, "tangentPropagation" : true});
        }
        {
            var Q0;
            Q0=qCreatedBy(id+"F8.planeOp",FACE);
            var sketch = newSketch(context, id + "F19", { "sketchPlane" : qUnion([Q0])});
            skLineSegment(sketch, "E24", {"start": v(141.75, 74.92) * mm, "end": v(148.07, 74.92) * mm, "construction": true});
            skLineSegment(sketch, "E25", {"start": v(142.7, 72.92) * mm, "end": v(148.7, 72.92) * mm});
            skLineSegment(sketch, "E26", {"start": v(148.7, 72.92) * mm, "end": v(148.7, 69.92) * mm});
            skLineSegment(sketch, "E27", {"start": v(148.7, 69.92) * mm, "end": v(143.7, 69.92) * mm});
            skLineSegment(sketch, "E28", {"start": v(143.7, 69.92) * mm, "end": v(143.7, 42.42) * mm});
            skLineSegment(sketch, "E29", {"start": v(143.7, 42.42) * mm, "end": v(148.7, 42.42) * mm});
            skLineSegment(sketch, "E30", {"start": v(148.7, 42.42) * mm, "end": v(148.7, 38.42) * mm});
            skLineSegment(sketch, "E31", {"start": v(148.7, 38.42) * mm, "end": v(142.7, 38.42) * mm});
            skLineSegment(sketch, "E32", {"start": v(142.7, 38.42) * mm, "end": v(142.7, 72.92) * mm});
            skSolve(sketch);
        }
        {
            var Q0;
            Q0=makeQuery(id+"F19.imprint","IMPRINT",FACE,{"disambiguationData":[TD([[makeQuery(id+"F19.imprint","IMPRINT",EDGE,{"derivedFrom":sQuery(id+"F19.wireOp",EDGE,"E25")}),-1.0]])]});
            var Q1;
            Q1=sQuery(id+"F19.wireOp",EDGE,"E24");
            revolve(context, id + "F20", {"entities" : qUnion([Q0]), "axis" : qUnion([Q1]), "revolveType" : RevolveType.FULL});
        }
        {
            var Q0;
            Q0=makeQuery(id+"F20.opRevolve","SWEPT_EDGE",EDGE,{"disambiguationData":[OSD([sQuery(id+"F19.wireOp",EDGE,"E30"),sQuery(id+"F19.wireOp",EDGE,"E31")])]});
            var Q1;
            Q1=makeQuery(id+"F20.opRevolve","SWEPT_EDGE",EDGE,{"disambiguationData":[OSD([sQuery(id+"F19.wireOp",EDGE,"E31"),sQuery(id+"F19.wireOp",EDGE,"E32")])]});
            fillet(context, id + "F21", {"entities" : qUnion([Q0, Q1]), "radius" : 1 * mm, "tangentPropagation" : true, "allowEdgeOverflow" : false});
        }
        {
            var Q0;
            Q0=makeQuery(id+"F20.opRevolve","SWEPT_FACE",FACE,{"disambiguationData":[OSD([sQuery(id+"F19.wireOp",EDGE,"E28")])]});
            var sketch = newSketch(context, id + "F22", { "sketchPlane" : qUnion([Q0])});
            skArc(sketch, "E33", {"start": v(-53.85, 53.24) * mm, "mid": v(-65.73, 61.79) * mm, "end": v(-80.32, 62.86) * mm});
            skFitSpline(sketch, "E34", {"points": [v(-53.85, 53.24) * mm, v(-56.84, 47.8) * mm, v(-65.91, 46.37) * mm, v(-69.9, 41.6) * mm], "startDerivative": vector(-6.96, -21.25) * mm, "endDerivative": vector(-9.27, -19.12) * mm});
            skArc(sketch, "E35", {"start": v(-69.24, 53.8) * mm, "mid": v(-73.8, 59.52) * mm, "end": v(-80.32, 62.86) * mm});
            skArc(sketch, "E36", {"start": v(-69.24, 53.8) * mm, "mid": v(-72.81, 54.31) * mm, "end": v(-76.39, 53.8) * mm});
            skArc(sketch, "E37", {"start": v(-70.85, 48.12) * mm, "mid": v(-73.34, 51.22) * mm, "end": v(-76.39, 53.8) * mm});
            skArc(sketch, "E38", {"start": v(-70.85, 48.12) * mm, "mid": v(-74.3, 48.4) * mm, "end": v(-76.52, 45.73) * mm});
            skArc(sketch, "E39", {"start": v(-69.9, 41.6) * mm, "mid": v(-72.54, 44.74) * mm, "end": v(-76.52, 45.73) * mm});
            skSolve(sketch);
        }
        {
            var Q0;
            Q0 = qSketchRegion(id + "F22", true);
            extrude(context, id + "F23", {"entities" : qUnion([Q0]), "oppositeDirection" : true, "depth" : 25.4 * mm});
        }
        {
            var Q0;
            Q0=makeQuery(id+"F23.opExtrude","SWEPT_EDGE",EDGE,{"disambiguationData":[OSD([sQuery(id+"F22.wireOp",EDGE,"E33"),sQuery(id+"F22.wireOp",EDGE,"E34")])]});
            var Q1;
            Q1=makeQuery(id+"F23.opExtrude","SWEPT_EDGE",EDGE,{"disambiguationData":[OSD([sQuery(id+"F22.wireOp",EDGE,"E34"),sQuery(id+"F22.wireOp",EDGE,"E39")])]});
            fillet(context, id + "F24", {"entities" : qUnion([Q0, Q1]), "radius" : 3 * mm, "tangentPropagation" : true, "allowEdgeOverflow" : false});
        }
        {
            var Q0;
            Q0=makeQuery(id+"F23.opExtrude","SWEPT_BODY",BODY,{"disambiguationData":[OSD([sQuery(id+"F22.wireOp",EDGE,"E33"),sQuery(id+"F22.wireOp",EDGE,"E34"),sQuery(id+"F22.wireOp",EDGE,"E35"),sQuery(id+"F22.wireOp",EDGE,"E36"),sQuery(id+"F22.wireOp",EDGE,"E37"),sQuery(id+"F22.wireOp",EDGE,"E38"),sQuery(id+"F22.wireOp",EDGE,"E39")])]});
            var Q1;
            Q1=makeQuery(id+"F20.opRevolve","SWEPT_EDGE",EDGE,{"disambiguationData":[OSD([sQuery(id+"F19.wireOp",EDGE,"E25"),sQuery(id+"F19.wireOp",EDGE,"E26")])]});
            circularPattern(context, id + "F25", {"entities" : qUnion([Q0]), "axis" : qUnion([Q1]), "angle" : 360 * degree, "instanceCount" : 5, "equalSpace" : true});
        }
        {
            var Q0;
            Q0=makeQuery(id+"F23.opExtrude","SWEPT_BODY",BODY,{"disambiguationData":[OSD([sQuery(id+"F22.wireOp",EDGE,"E33"),sQuery(id+"F22.wireOp",EDGE,"E34"),sQuery(id+"F22.wireOp",EDGE,"E35"),sQuery(id+"F22.wireOp",EDGE,"E36"),sQuery(id+"F22.wireOp",EDGE,"E37"),sQuery(id+"F22.wireOp",EDGE,"E38"),sQuery(id+"F22.wireOp",EDGE,"E39")])]});
            var Q1;
            Q1=makeQuery(id+"F25.opPattern","COPY",BODY,{"derivedFrom":makeQuery(id+"F23.opExtrude","SWEPT_BODY",BODY,{"disambiguationData":[OSD([sQuery(id+"F22.wireOp",EDGE,"E33"),sQuery(id+"F22.wireOp",EDGE,"E34"),sQuery(id+"F22.wireOp",EDGE,"E35"),sQuery(id+"F22.wireOp",EDGE,"E36"),sQuery(id+"F22.wireOp",EDGE,"E37"),sQuery(id+"F22.wireOp",EDGE,"E38"),sQuery(id+"F22.wireOp",EDGE,"E39")])]}),"instanceName":"4"});
            var Q2;
            Q2=makeQuery(id+"F25.opPattern","COPY",BODY,{"derivedFrom":makeQuery(id+"F23.opExtrude","SWEPT_BODY",BODY,{"disambiguationData":[OSD([sQuery(id+"F22.wireOp",EDGE,"E33"),sQuery(id+"F22.wireOp",EDGE,"E34"),sQuery(id+"F22.wireOp",EDGE,"E35"),sQuery(id+"F22.wireOp",EDGE,"E36"),sQuery(id+"F22.wireOp",EDGE,"E37"),sQuery(id+"F22.wireOp",EDGE,"E38"),sQuery(id+"F22.wireOp",EDGE,"E39")])]}),"instanceName":"1"});
            var Q3;
            Q3=makeQuery(id+"F25.opPattern","COPY",BODY,{"derivedFrom":makeQuery(id+"F23.opExtrude","SWEPT_BODY",BODY,{"disambiguationData":[OSD([sQuery(id+"F22.wireOp",EDGE,"E33"),sQuery(id+"F22.wireOp",EDGE,"E34"),sQuery(id+"F22.wireOp",EDGE,"E35"),sQuery(id+"F22.wireOp",EDGE,"E36"),sQuery(id+"F22.wireOp",EDGE,"E37"),sQuery(id+"F22.wireOp",EDGE,"E38"),sQuery(id+"F22.wireOp",EDGE,"E39")])]}),"instanceName":"2"});
            var Q4;
            Q4=makeQuery(id+"F25.opPattern","COPY",BODY,{"derivedFrom":makeQuery(id+"F23.opExtrude","SWEPT_BODY",BODY,{"disambiguationData":[OSD([sQuery(id+"F22.wireOp",EDGE,"E33"),sQuery(id+"F22.wireOp",EDGE,"E34"),sQuery(id+"F22.wireOp",EDGE,"E35"),sQuery(id+"F22.wireOp",EDGE,"E36"),sQuery(id+"F22.wireOp",EDGE,"E37"),sQuery(id+"F22.wireOp",EDGE,"E38"),sQuery(id+"F22.wireOp",EDGE,"E39")])]}),"instanceName":"3"});
            var Q5;
            Q5=makeQuery(id+"F20.opRevolve","SWEPT_BODY",BODY,{"disambiguationData":[OSD([sQuery(id+"F19.wireOp",EDGE,"E25"),sQuery(id+"F19.wireOp",EDGE,"E26"),sQuery(id+"F19.wireOp",EDGE,"E27"),sQuery(id+"F19.wireOp",EDGE,"E28"),sQuery(id+"F19.wireOp",EDGE,"E29"),sQuery(id+"F19.wireOp",EDGE,"E30"),sQuery(id+"F19.wireOp",EDGE,"E31"),sQuery(id+"F19.wireOp",EDGE,"E32")])]});
            booleanBodies(context, id + "F26", {"operationType" : BooleanOperationType.SUBTRACTION, "tools" : qUnion([Q0, Q1, Q2, Q3, Q4]), "targets" : qUnion([Q5])});
        }
        {
            var Q0;
            Q0=qCreatedBy(id+"F8.planeOp",FACE);
            var sketch = newSketch(context, id + "F27", { "sketchPlane" : qUnion([Q0])});
            skLineSegment(sketch, "E40.bottom", {"start": v(-17.5, 117.5) * mm, "end": v(17.5, 117.5) * mm});
            skLineSegment(sketch, "E40.top", {"start": v(-17.5, 107.5) * mm, "end": v(17.5, 107.5) * mm, "construction": true});
            skLineSegment(sketch, "E40.left", {"start": v(-17.5, 117.5) * mm, "end": v(-17.5, 107.5) * mm});
            skLineSegment(sketch, "E40.right", {"start": v(17.5, 117.5) * mm, "end": v(17.5, 107.5) * mm});
            skArc(sketch, "E41", {"start": v(-17.5, 107.5) * mm, "mid": v(0, 97.5) * mm, "end": v(17.5, 107.5) * mm});
            skSolve(sketch);
        }
        {
            var Q0;
            Q0=makeQuery(id+"F27.imprint","IMPRINT",FACE,{"disambiguationData":[TD([[makeQuery(id+"F27.imprint","IMPRINT",EDGE,{"derivedFrom":sQuery(id+"F27.wireOp",EDGE,"E40.bottom")}),-1.0]])]});
            extrude(context, id + "F28", {"entities" : qUnion([Q0]), "depth" : 6 * mm, "hasSecondDirection" : true, "secondDirectionOppositeDirection" : true, "secondDirectionDepth" : 15 * mm});
        }
        {
            var Q0;
            Q0=qCreatedBy(makeId("Right.planeOp"),FACE);
            var sketch = newSketch(context, id + "F29", { "sketchPlane" : qUnion([Q0])});
            skLineSegment(sketch, "E42.0.0", {"start": v(-111.5, 39.5) * mm, "end": v(-117.5, 39.5) * mm});
            skFitSpline(sketch, "E42.0.5", {"points": [v(-40.18, 39.5) * mm, v(-38.8, 39.5) * mm, v(-37.4, 39.5) * mm, v(-36.01, 39.5) * mm]});
            skLineSegment(sketch, "E42.0.6", {"start": v(-36.01, 39.5) * mm, "end": v(39.5, 39.5) * mm});
            skFitSpline(sketch, "E42.0.7", {"points": [v(-36.01, 39.5) * mm, v(-37.4, 39.5) * mm, v(-38.8, 39.5) * mm, v(-40.18, 39.5) * mm]});
            skLineSegment(sketch, "E43.0.0", {"start": v(-35.97, 33.5) * mm, "end": v(39.5, 33.5) * mm});
            skLineSegment(sketch, "E43.0.1", {"start": v(-35.97, 33.5) * mm, "end": v(-39.54, 33.5) * mm});
            skLineSegment(sketch, "E43.0.4", {"start": v(-111.5, 33.5) * mm, "end": v(-117.5, 33.5) * mm});
            skLineSegment(sketch, "E43.0.6", {"start": v(-117.5, 33.5) * mm, "end": v(-111.5, 33.5) * mm});
            skLineSegment(sketch, "E43.0.9", {"start": v(-39.54, 33.5) * mm, "end": v(-35.97, 33.5) * mm});
            skLineSegment(sketch, "E44.0.3", {"start": v(-111.5, 33.5) * mm, "end": v(-111.5, 39.5) * mm});
            skLineSegment(sketch, "E45", {"start": v(-117.5, 33.5) * mm, "end": v(-117.5, 39.5) * mm});
            skSolve(sketch);
        }
        {
            var Q0;
            Q0 = qSketchRegion(id + "F29", true);
            extrude(context, id + "F30", {"entities" : qUnion([Q0]), "operationType" : NewBodyOperationType.REMOVE, "endBound" : BoundingType.THROUGH_ALL, "oppositeDirection" : true, "depth" : 25.4 * mm, "hasSecondDirection" : true, "secondDirectionBound" : SecondDirectionBoundingType.THROUGH_ALL, "secondDirectionOppositeDirection" : false, "secondDirectionDepth" : 25.4 * mm});
        }
        {
            var Q0;
            Q0=makeQuery(id+"F28.opExtrude","CAP_FACE",FACE,{"disambiguationData":[OSD([sQuery(id+"F27.wireOp",EDGE,"E40.bottom"),sQuery(id+"F27.wireOp",EDGE,"E40.left"),sQuery(id+"F27.wireOp",EDGE,"E40.right"),sQuery(id+"F27.wireOp",EDGE,"E41")])],"isStart":true});
            var sketch = newSketch(context, id + "F31", { "sketchPlane" : qUnion([Q0])});
            skEllipse(sketch, "E46", {"center": v(0, -112.5) * mm, "majorRadius": 10 * mm, "minorRadius": 6 * mm, "majorAxis": v(-1, 0)});
            skPoint(sketch, "E46.centerSnap0", {"position": v(0, -117.5) * mm});
            skLineSegment(sketch, "E47", {"start": v(5.53, -117.5) * mm, "end": v(-5.53, -117.5) * mm});
            skSolve(sketch);
        }
        {
            var Q0;
            {var subQ0=sQuery(id+"F31.wireOp",EDGE,"E47");Q0=makeQuery(id+"F31.imprint","IMPRINT",FACE,{"disambiguationData":[TD([[makeQuery(id+"F31.imprint","IMPRINT",EDGE,{"derivedFrom":subQ0}),1.0]])]});}
            extrude(context, id + "F32", {"entities" : qUnion([Q0]), "operationType" : NewBodyOperationType.ADD, "depth" : 15 * mm});
        }
        {
            var Q0;
            {var subQ0=sQuery(id+"F31.wireOp",EDGE,"E47");var subQ1=sQuery(id+"F31.wireOp",EDGE,"E46");var subQ2=sQuery(id+"F27.wireOp",EDGE,"E40.bottom");Q0=makeQuery(id+"F32.opExtrude","SWEPT_EDGE",EDGE,{"disambiguationData":[OSD([subQ2,subQ1,subQ0]),TDD([makeQuery(id+"F31.imprint","INTERSECT",VERTEX,{"disambiguationData":[OD(0.0)],"derivedFrom":[makeQuery(id+"F28.opExtrude","CAP_EDGE",EDGE,{"disambiguationData":[OSD([subQ2])],"isStart":true}),subQ1,subQ0]})])]});}
            var Q1;
            {var subQ0=sQuery(id+"F31.wireOp",EDGE,"E47");var subQ1=sQuery(id+"F31.wireOp",EDGE,"E46");var subQ2=sQuery(id+"F27.wireOp",EDGE,"E40.bottom");Q1=makeQuery(id+"F32.opExtrude","SWEPT_EDGE",EDGE,{"disambiguationData":[OSD([subQ2,subQ1,subQ0]),TDD([makeQuery(id+"F31.imprint","INTERSECT",VERTEX,{"disambiguationData":[OD(1.0)],"derivedFrom":[makeQuery(id+"F28.opExtrude","CAP_EDGE",EDGE,{"disambiguationData":[OSD([subQ2])],"isStart":true}),subQ1,subQ0]})])]});}
            fillet(context, id + "F33", {"entities" : qUnion([Q0, Q1]), "radius" : 6 * mm, "tangentPropagation" : true, "allowEdgeOverflow" : false});
        }
        {
            var Q0;
            Q0=makeQuery(id+"F32.opExtrude","CAP_EDGE",EDGE,{"disambiguationData":[OSD([sQuery(id+"F31.wireOp",EDGE,"E46")])],"isStart":false});
            fillet(context, id + "F34", {"entities" : qUnion([Q0]), "radius" : 3 * mm, "tangentPropagation" : true, "allowEdgeOverflow" : false});
        }
        {
            var Q0;
            Q0=qCreatedBy(makeId("Right.planeOp"),FACE);
            var sketch = newSketch(context, id + "F35", { "sketchPlane" : qUnion([Q0])});
            skCircle(sketch, "E48", {"center": v(-112.5, 70.5) * mm, "radius": 5 * mm});
            skLineSegment(sketch, "E49", {"start": v(-112.5, 75.5) * mm, "end": v(-112.5, 65.5) * mm});
            skSolve(sketch);
        }
        {
            var Q0;
            {var subQ0=sQuery(id+"F35.wireOp",EDGE,"E49");Q0=makeQuery(id+"F35.imprint","IMPRINT",FACE,{"disambiguationData":[TD([[makeQuery(id+"F35.imprint","IMPRINT",EDGE,{"derivedFrom":subQ0}),1.0]])]});}
            var Q1;
            Q1=sQuery(id+"F35.wireOp",EDGE,"E49");
            revolve(context, id + "F36", {"operationType" : NewBodyOperationType.ADD, "entities" : qUnion([Q0]), "axis" : qUnion([Q1]), "revolveType" : RevolveType.FULL});
        }
    });
